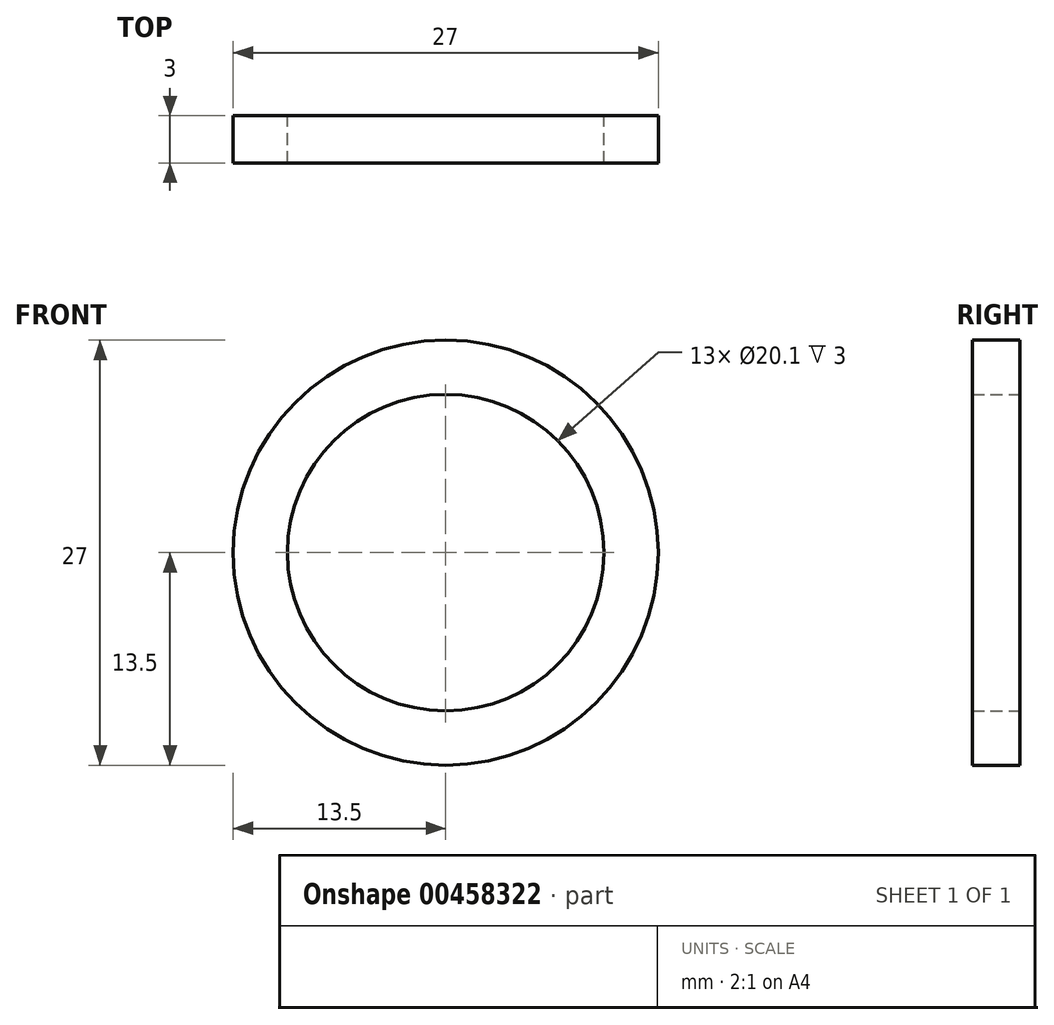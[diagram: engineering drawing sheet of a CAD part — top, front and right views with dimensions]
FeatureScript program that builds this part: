
annotation { "Feature Type Name" : "Feature", "Feature Type Description" : "" }
export const myFeature = defineFeature(function(context is Context, id is Id, definition is map)
    precondition{}
    {
        {
            var Q0;
            Q0=qCreatedBy(makeId("Front.planeOp"),FACE);
            var sketch = newSketch(context, id + "F0", { "sketchPlane" : qUnion([Q0])});
            skCircle(sketch, "E0", {"center": v(0, 0) * mm, "radius": 13.5 * mm});
            skCircle(sketch, "E1", {"center": v(0, 0) * mm, "radius": 10.05 * mm});
            skSolve(sketch);
        }
        {
            var Q0;
            Q0 = qSketchRegion(id + "F0", true);
            extrude(context, id + "F1", {"entities" : qUnion([Q0]), "depth" : 3 * mm});
        }
    });
